# Revit family: Gira_028427
name_source: partatom
category: Electrical Fixtures
revit_build: Autodesk Revit 2017 (Build: 20160225_1515(x64)
units: mm (PartAtom-declared; Revit-internal decimal feet)

## family parameters
Cut with Voids When Loaded = No
Host = Face
Maintain Annotation Orientation = No
Part Type = Normal
Room Calculation Point = No
Round Connector Dimension = Use Diameter
Shared = No

## types (1)
- Abd. BSF UAE/IAE + Netzwerk System 55 Reinweiß m
    Ausführung der Oberfläche = matt
    Available = Yes
    Befestigungsart = Befestigung mit Schraube
    Beschriftungsfeld = mit Beschriftungsfeld
    Category = Einsatz/Abdeckung für Kommunikationstechnik
    Data sheet (1) = https://katalog.gira.de
    Default Elevation = 1219 mm
    Farbe = weiß
    GTIN = 4010337284277
    Geeignet für Schutzart (IP) = IP20
    HAN = 028427
    Halogenfrei = Yes
    HeinzeBIM = https://bimportal.heinze.de
    Keynote = Sys55_Abdeckung_Schalten und Tasten
    Lüsterklemme = No
    Manufacturer URL = https://www.gira.de
    Mit Aufdruck = No
    Mit Klappdeckel = No
    Mit Staubschutz = No
    Mit Zugentlastung = No
    Montageart = unter Putz
    Name = Abd. BSF UAE/IAE + Netzwerk System 55 Reinweiß m
    Oberfläche = sonstige
    RAL-Nummer (ähnlich) = 9010
    Region = DE
    Tragring = No
    Transparent = No
    URL = http://katalog.gira.de
    Verwendung = UAE/IAE
    Werkstoff = Kunststoff
    Werkstoffgüte = sonstige
    Zusammenstellung = Zentralplatte

## geometry (parser evidence)
native form markers: Blend x2, Sweep x9
no freeform markers — native parametric forms only
